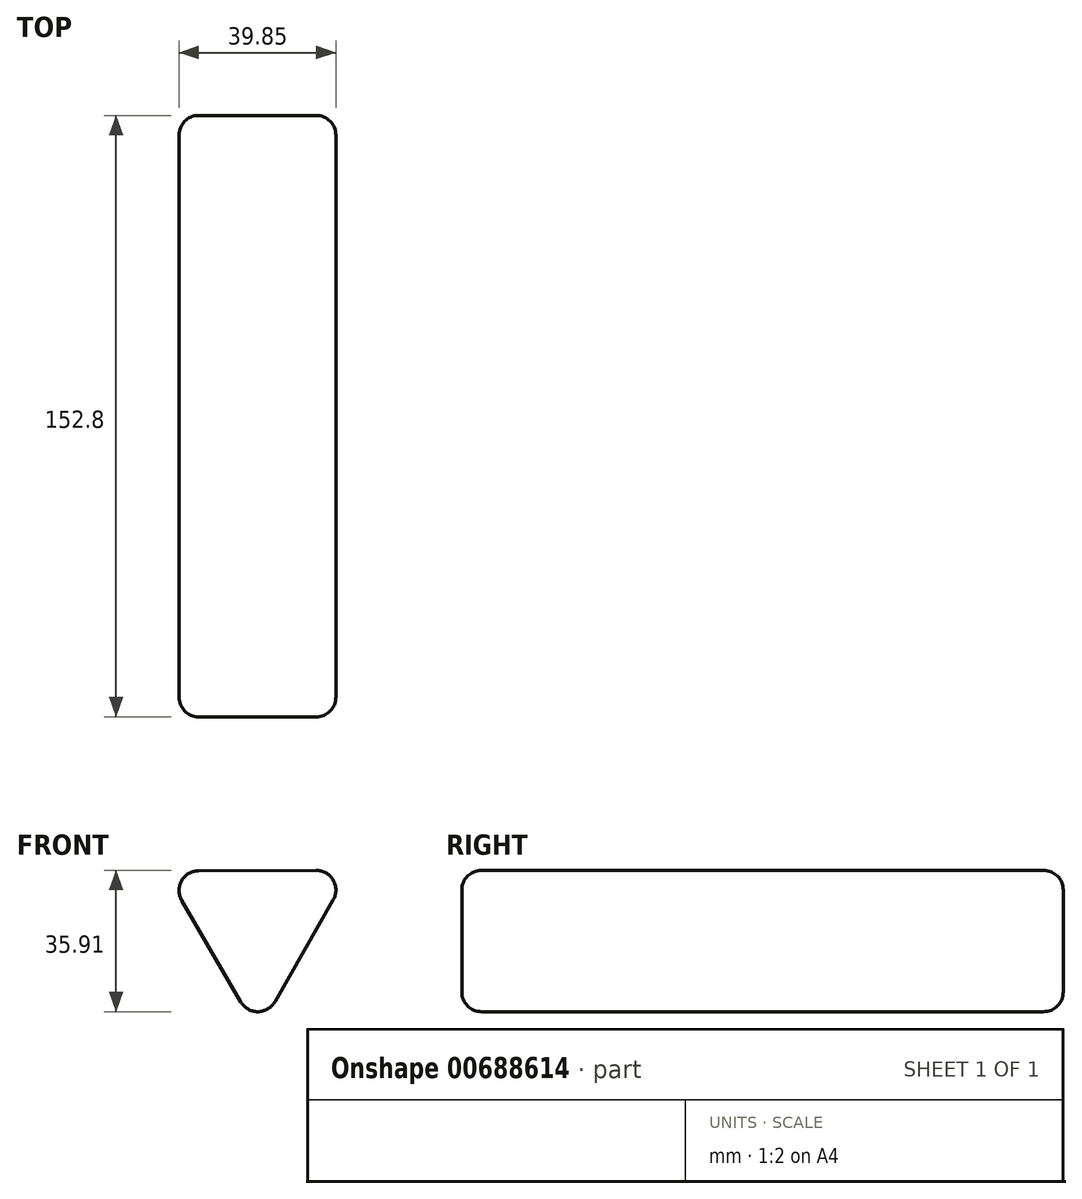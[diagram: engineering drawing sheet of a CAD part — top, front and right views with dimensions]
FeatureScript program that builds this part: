
annotation { "Feature Type Name" : "Feature", "Feature Type Description" : "" }
export const myFeature = defineFeature(function(context is Context, id is Id, definition is map)
    precondition{}
    {
        {
            var Q0;
            Q0=qCreatedBy(makeId("Front.planeOp"),FACE);
            var sketch = newSketch(context, id + "F0", { "sketchPlane" : qUnion([Q0])});
            skLineSegment(sketch, "E0.0", {"start": v(-23.2, 12.52) * mm, "end": v(23.96, 12.7) * mm});
            skLineSegment(sketch, "E0.1", {"start": v(23.96, 12.7) * mm, "end": v(0.54, -28.24) * mm});
            skLineSegment(sketch, "E0.2", {"start": v(0.54, -28.24) * mm, "end": v(-23.2, 12.52) * mm});
            skSolve(sketch);
        }
        {
            var Q0;
            Q0=makeQuery(id+"F0.imprint","IMPRINT",FACE,{"disambiguationData":[TD([[makeQuery(id+"F0.imprint","IMPRINT",EDGE,{"derivedFrom":sQuery(id+"F0.wireOp",EDGE,"E0.0")}),-1.0]])]});
            extrude(context, id + "F1", {"entities" : qUnion([Q0]), "endBound" : BoundingType.SYMMETRIC, "depth" : 152.8 * mm, "offsetDistance" : 25 * mm});
        }
        {
            var Q0;
            Q0=makeQuery(id+"F1.opExtrude","CAP_FACE",FACE,{"disambiguationData":[OSD([sQuery(id+"F0.wireOp",EDGE,"E0.0"),sQuery(id+"F0.wireOp",EDGE,"E0.1"),sQuery(id+"F0.wireOp",EDGE,"E0.2")])],"isStart":false});
            var Q1;
            Q1=makeQuery(id+"F1.opExtrude","CAP_FACE",FACE,{"disambiguationData":[OSD([sQuery(id+"F0.wireOp",EDGE,"E0.0"),sQuery(id+"F0.wireOp",EDGE,"E0.1"),sQuery(id+"F0.wireOp",EDGE,"E0.2")])],"isStart":true});
            var Q2;
            Q2=makeQuery(id+"F1.opExtrude","SWEPT_EDGE",EDGE,{"disambiguationData":[OSD([sQuery(id+"F0.wireOp",EDGE,"E0.0"),sQuery(id+"F0.wireOp",EDGE,"E0.2")])]});
            var Q3;
            Q3=makeQuery(id+"F1.opExtrude","SWEPT_EDGE",EDGE,{"disambiguationData":[OSD([sQuery(id+"F0.wireOp",EDGE,"E0.1"),sQuery(id+"F0.wireOp",EDGE,"E0.2")])]});
            var Q4;
            Q4=makeQuery(id+"F1.opExtrude","SWEPT_EDGE",EDGE,{"disambiguationData":[OSD([sQuery(id+"F0.wireOp",EDGE,"E0.0"),sQuery(id+"F0.wireOp",EDGE,"E0.1")])]});
            fillet(context, id + "F2", {"entities" : qUnion([Q0, Q1, Q2, Q3, Q4]), "radius" : 5 * mm, "tangentPropagation" : true, "allowEdgeOverflow" : false});
        }
    });
